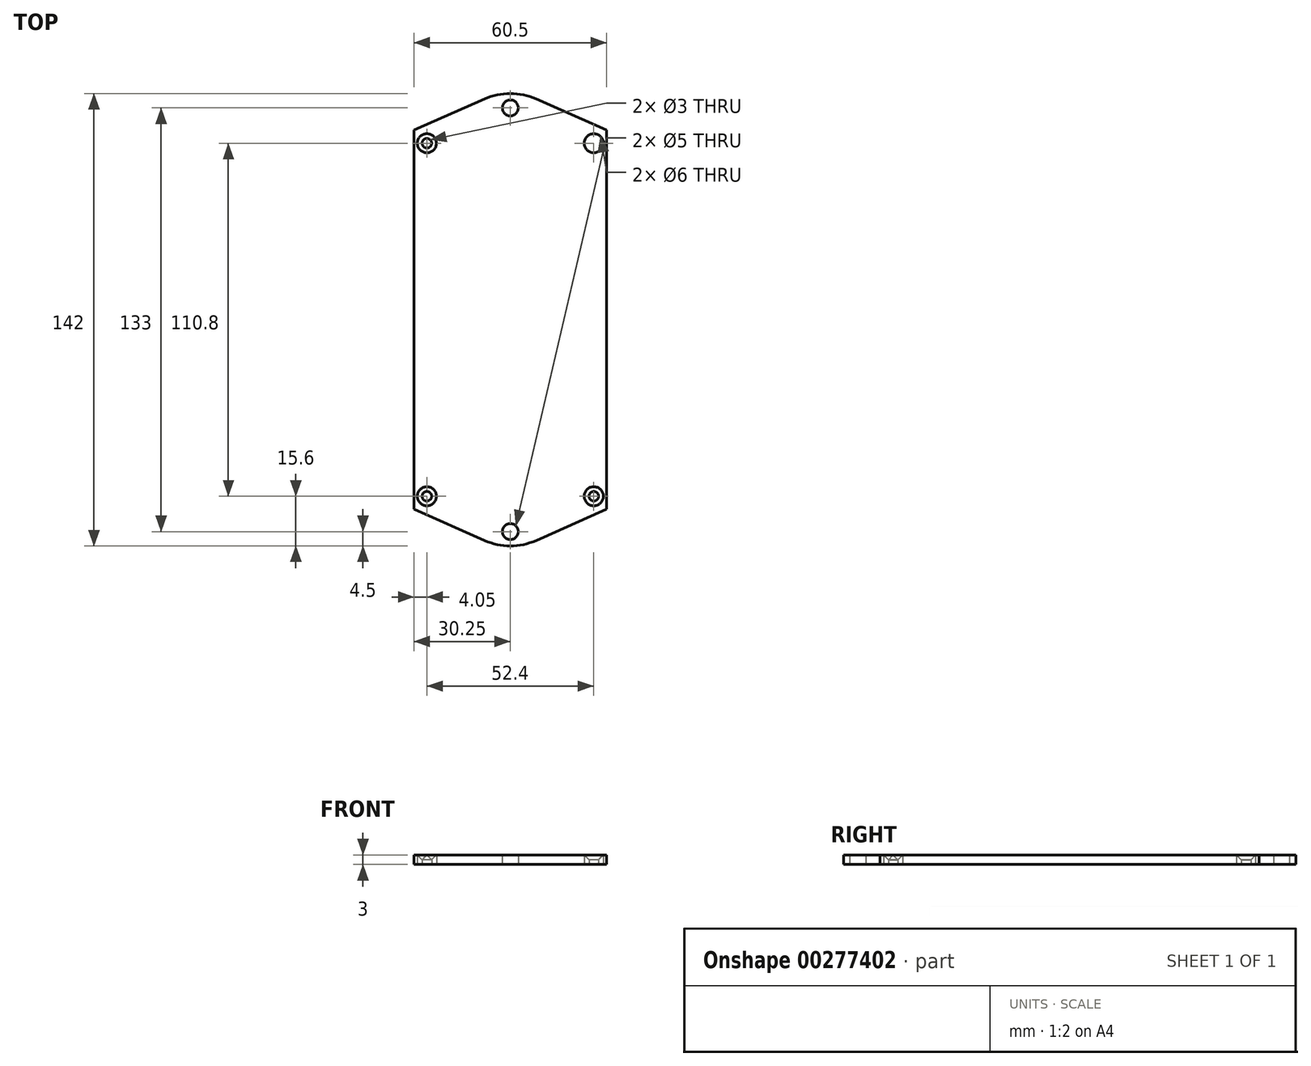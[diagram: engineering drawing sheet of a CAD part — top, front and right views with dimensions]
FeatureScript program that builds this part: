
annotation { "Feature Type Name" : "Feature", "Feature Type Description" : "" }
export const myFeature = defineFeature(function(context is Context, id is Id, definition is map)
    precondition{}
    {
        {
            var Q0;
            Q0=qCreatedBy(makeId("Top.planeOp"),FACE);
            var sketch = newSketch(context, id + "F0", { "sketchPlane" : qUnion([Q0])});
            skLineSegment(sketch, "E0.bottom", {"start": v(-30.25, 59.5) * mm, "end": v(30.25, 59.5) * mm});
            skLineSegment(sketch, "E0.top", {"start": v(-30.25, -59.5) * mm, "end": v(30.25, -59.5) * mm});
            skLineSegment(sketch, "E0.left", {"start": v(-30.25, 59.5) * mm, "end": v(-30.25, -59.5) * mm});
            skLineSegment(sketch, "E0.right", {"start": v(30.25, 59.5) * mm, "end": v(30.25, -59.5) * mm});
            skPoint(sketch, "E0.middle", {"position": v(0, 0) * mm});
            skCircle(sketch, "E1", {"center": v(-26.2, 55.4) * mm, "radius": 1.5 * mm});
            skCircle(sketch, "E2", {"center": v(-26.2, 55.4) * mm, "radius": 3 * mm});
            skCircle(sketch, "E3.MirrorC", {"center": v(26.2, 55.4) * mm, "radius": 1.5 * mm});
            skCircle(sketch, "E4.MirrorC", {"center": v(26.2, 55.4) * mm, "radius": 3 * mm});
            skCircle(sketch, "E5.MirrorC", {"center": v(26.2, -55.4) * mm, "radius": 1.5 * mm});
            skCircle(sketch, "E6.MirrorC", {"center": v(26.2, -55.4) * mm, "radius": 3 * mm});
            skCircle(sketch, "E7.MirrorC", {"center": v(-26.2, -55.4) * mm, "radius": 1.5 * mm});
            skCircle(sketch, "E8.MirrorC", {"center": v(-26.2, -55.4) * mm, "radius": 3 * mm});
            skLineSegment(sketch, "E9", {"start": v(-30.25, 59.5) * mm, "end": v(-8.08, 69.3) * mm});
            skLineSegment(sketch, "E10", {"start": v(8.08, 69.3) * mm, "end": v(30.25, 59.5) * mm});
            skPoint(sketch, "E11.visualSharp", {"position": v(0, 72.87) * mm});
            skArc(sketch, "E11.filletArc", {"start": v(8.08, 69.3) * mm, "mid": v(0, 71) * mm, "end": v(-8.08, 69.3) * mm});
            skCircle(sketch, "E12", {"center": v(0, 66.5) * mm, "radius": 2.5 * mm});
            skCircle(sketch, "E13.MirrorC", {"center": v(0, -66.5) * mm, "radius": 2.5 * mm});
            skLineSegment(sketch, "E14.MirrorCS", {"start": v(-30.25, -59.5) * mm, "end": v(-8.08, -69.3) * mm});
            skLineSegment(sketch, "E15.MirrorCS", {"start": v(8.08, -69.3) * mm, "end": v(30.25, -59.5) * mm});
            skArc(sketch, "E16.MirrorCS", {"start": v(8.08, -69.3) * mm, "mid": v(0, -71) * mm, "end": v(-8.08, -69.3) * mm});
            skSolve(sketch);
        }
        {
            var Q0;
            Q0=makeQuery(id+"F0.imprint","IMPRINT",FACE,{"disambiguationData":[TD([[makeQuery(id+"F0.imprint","IMPRINT",EDGE,{"derivedFrom":sQuery(id+"F0.wireOp",EDGE,"E0.bottom")}),-1.0]])]});
            var Q1;
            Q1=makeQuery(id+"F0.imprint","IMPRINT",FACE,{"disambiguationData":[TD([[makeQuery(id+"F0.imprint","IMPRINT",EDGE,{"derivedFrom":sQuery(id+"F0.wireOp",EDGE,"E0.bottom")}),1.0]])]});
            var Q2;
            Q2=makeQuery(id+"F0.imprint","IMPRINT",FACE,{"disambiguationData":[TD([[makeQuery(id+"F0.imprint","IMPRINT",EDGE,{"derivedFrom":sQuery(id+"F0.wireOp",EDGE,"E0.top")}),-1.0]])]});
            var Q3;
            Q3=makeQuery(id+"F0.imprint","IMPRINT",FACE,{"disambiguationData":[TD([[makeQuery(id+"F0.imprint","IMPRINT",EDGE,{"derivedFrom":sQuery(id+"F0.wireOp",EDGE,"E1")}),-1.0]])]});
            var Q4;
            Q4=makeQuery(id+"F0.imprint","IMPRINT",FACE,{"disambiguationData":[TD([[makeQuery(id+"F0.imprint","IMPRINT",EDGE,{"derivedFrom":sQuery(id+"F0.wireOp",EDGE,"E4.MirrorC")}),-1.0]])]});
            var Q5;
            Q5=makeQuery(id+"F0.imprint","IMPRINT",FACE,{"disambiguationData":[TD([[makeQuery(id+"F0.imprint","IMPRINT",EDGE,{"derivedFrom":sQuery(id+"F0.wireOp",EDGE,"E7.MirrorC")}),1.0]])]});
            var Q6;
            Q6=makeQuery(id+"F0.imprint","IMPRINT",FACE,{"disambiguationData":[TD([[makeQuery(id+"F0.imprint","IMPRINT",EDGE,{"derivedFrom":sQuery(id+"F0.wireOp",EDGE,"E5.MirrorC")}),-1.0]])]});
            extrude(context, id + "F1", {"entities" : qUnion([Q0, Q1, Q2, Q3, Q4, Q5, Q6]), "depth" : 3 * mm});
        }
        {
            var Q0;
            Q0=makeQuery(id+"F1.opExtrude","CAP_EDGE",EDGE,{"disambiguationData":[OSD([sQuery(id+"F0.wireOp",EDGE,"E1")])],"isStart":false});
            var Q1;
            Q1=makeQuery(id+"F1.opExtrude","CAP_EDGE",EDGE,{"disambiguationData":[OSD([sQuery(id+"F0.wireOp",EDGE,"E3.MirrorC")])],"isStart":false});
            var Q2;
            Q2=makeQuery(id+"F1.opExtrude","CAP_EDGE",EDGE,{"disambiguationData":[OSD([sQuery(id+"F0.wireOp",EDGE,"E5.MirrorC")])],"isStart":false});
            var Q3;
            Q3=makeQuery(id+"F1.opExtrude","CAP_EDGE",EDGE,{"disambiguationData":[OSD([sQuery(id+"F0.wireOp",EDGE,"E7.MirrorC")])],"isStart":false});
            chamfer(context, id + "F2", {"entities" : qUnion([Q0, Q1, Q2, Q3]), "width" : 1.5 * mm, "tangentPropagation" : true});
        }
    });
